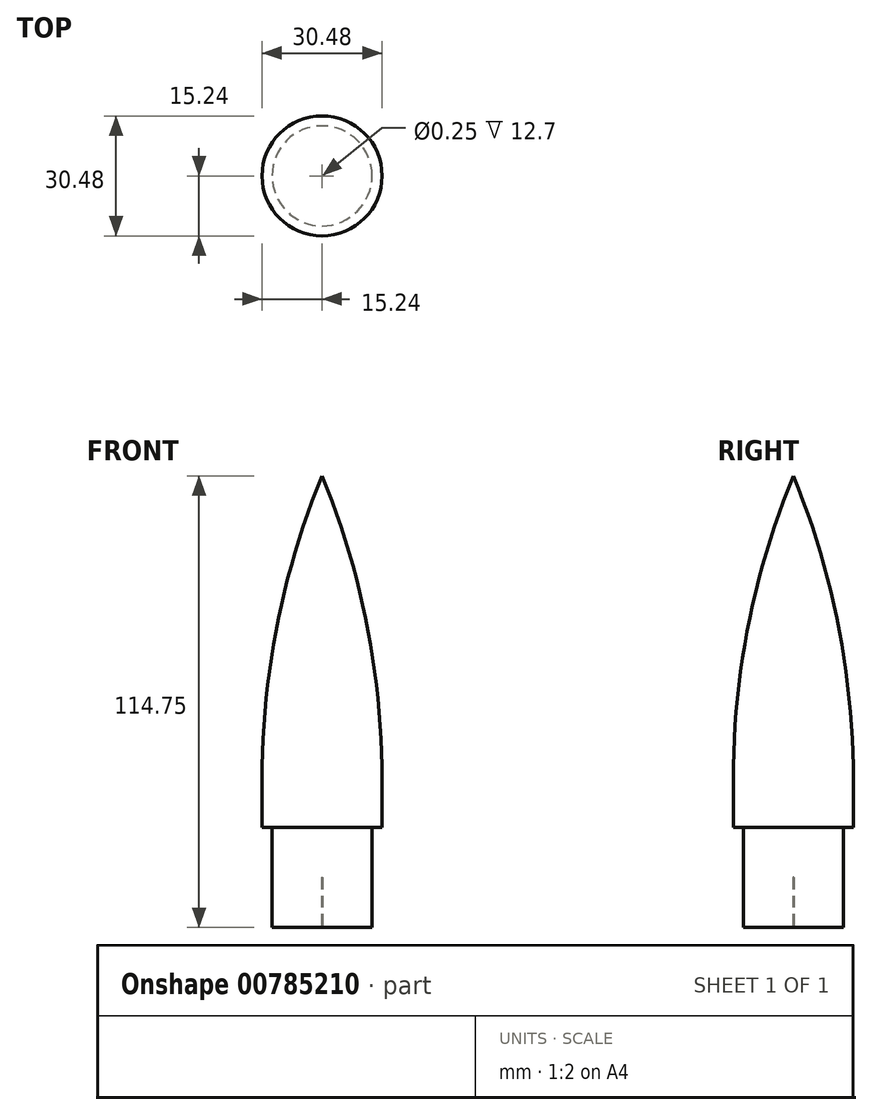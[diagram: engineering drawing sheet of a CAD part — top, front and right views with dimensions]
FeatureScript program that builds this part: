
annotation { "Feature Type Name" : "Feature", "Feature Type Description" : "" }
export const myFeature = defineFeature(function(context is Context, id is Id, definition is map)
    precondition{}
    {
        {
            var Q0;
            Q0=qCreatedBy(makeId("Front.planeOp"),FACE);
            var sketch = newSketch(context, id + "F0", { "sketchPlane" : qUnion([Q0])});
            skLineSegment(sketch, "E0", {"start": v(-12.7, 114.75) * mm, "end": v(-12.7, 0) * mm});
            skLineSegment(sketch, "E1", {"start": v(-12.7, 0) * mm, "end": v(0, 0) * mm});
            skLineSegment(sketch, "E2", {"start": v(0, 0) * mm, "end": v(0, 25.4) * mm});
            skLineSegment(sketch, "E3", {"start": v(0, 25.4) * mm, "end": v(2.54, 25.4) * mm});
            skLineSegment(sketch, "E4", {"start": v(-12.7, 0) * mm, "end": v(-12.7, -12.46) * mm, "construction": true});
            skLineSegment(sketch, "E5", {"start": v(2.54, 25.4) * mm, "end": v(2.54, 37.66) * mm});
            skArc(sketch, "E6", {"start": v(2.54, 37.66) * mm, "mid": v(-1.3, 76.95) * mm, "end": v(-12.7, 114.75) * mm});
            skSolve(sketch);
        }
        {
            var Q0;
            Q0=makeQuery(id+"F0.imprint","IMPRINT",FACE,{"disambiguationData":[TD([[makeQuery(id+"F0.imprint","IMPRINT",EDGE,{"derivedFrom":sQuery(id+"F0.wireOp",EDGE,"E0")}),1.0]])]});
            var Q1;
            Q1=sQuery(id+"F0.wireOp",EDGE,"E4");
            revolve(context, id + "F1", {"surfaceOperationType" : NewSurfaceOperationType.NEW, "entities" : qUnion([Q0]), "axis" : qUnion([Q1]), "revolveType" : RevolveType.FULL});
        }
        {
            var Q0;
            Q0=makeQuery(id+"F1.opRevolve","SWEPT_FACE",FACE,{"disambiguationData":[OSD([sQuery(id+"F0.wireOp",EDGE,"E1")])]});
            var sketch = newSketch(context, id + "F2", { "sketchPlane" : qUnion([Q0])});
            skCircle(sketch, "E7", {"center": v(-12.7, 0) * mm, "radius": 0.13 * mm});
            skSolve(sketch);
        }
        {
            var Q0;
            Q0 = qSketchRegion(id + "F2", true);
            extrude(context, id + "F3", {"entities" : qUnion([Q0]), "operationType" : NewBodyOperationType.REMOVE, "oppositeDirection" : true, "depth" : 12.7 * mm, "offsetDistance" : 25.4 * mm});
        }
    });
